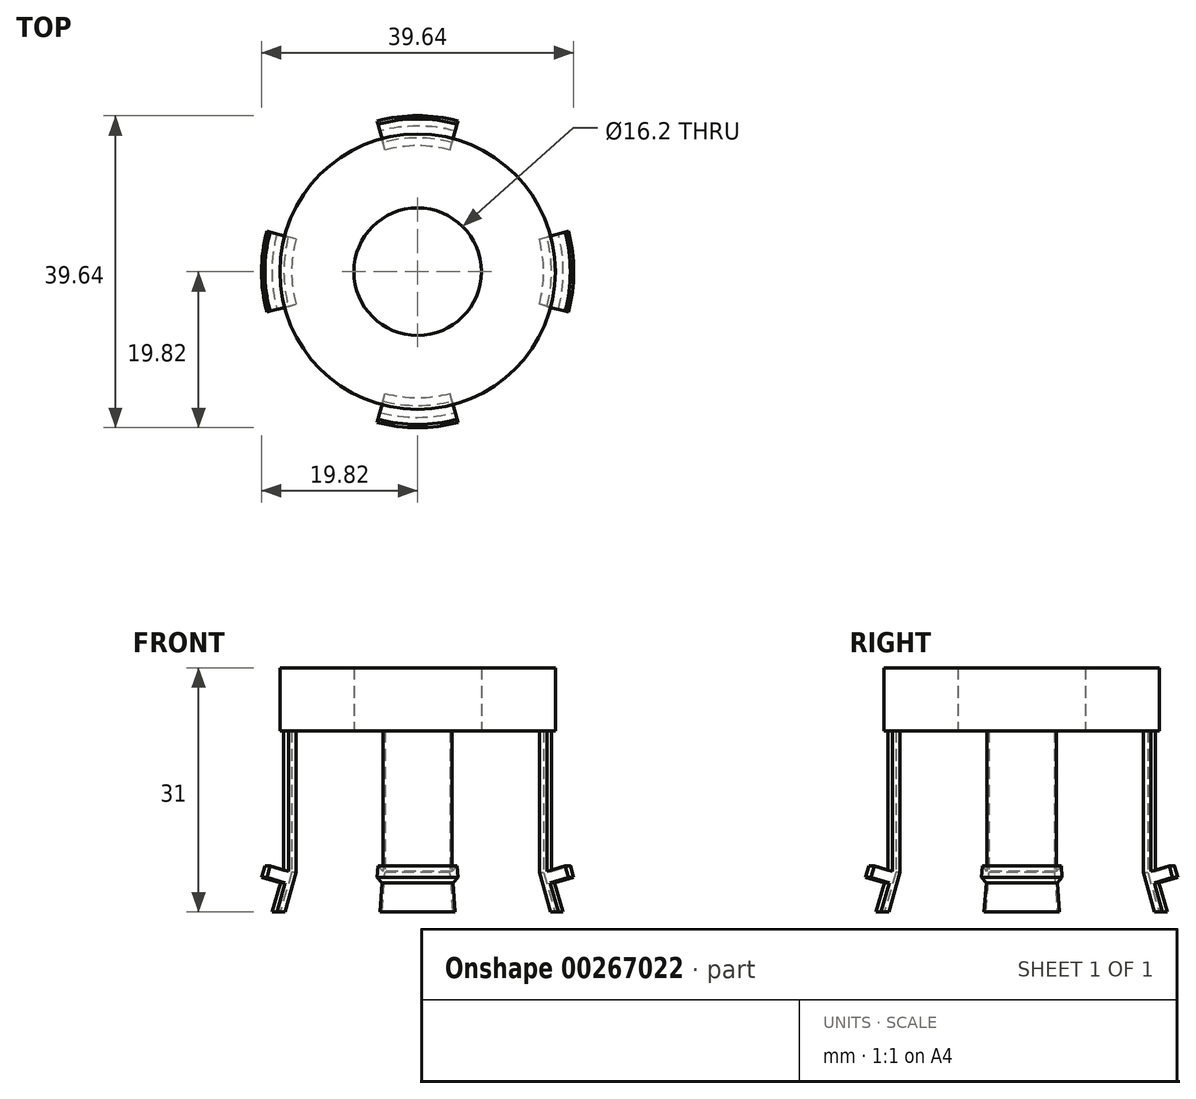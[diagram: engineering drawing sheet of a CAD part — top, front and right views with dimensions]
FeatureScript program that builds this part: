
annotation { "Feature Type Name" : "Feature", "Feature Type Description" : "" }
export const myFeature = defineFeature(function(context is Context, id is Id, definition is map)
    precondition{}
    {
        {
            var Q0;
            Q0=qCreatedBy(makeId("Front.planeOp"),FACE);
            var sketch = newSketch(context, id + "F0", { "sketchPlane" : qUnion([Q0])});
            skLineSegment(sketch, "E0", {"start": v(0, -11.42) * mm, "end": v(0, 25.7) * mm, "construction": true});
            skLineSegment(sketch, "E1", {"start": v(-16, 23) * mm, "end": v(-16, 5) * mm});
            skLineSegment(sketch, "E2", {"start": v(-16, 5) * mm, "end": v(-17.46, 0) * mm});
            skLineSegment(sketch, "E3", {"start": v(-17.46, 0) * mm, "end": v(-18.5, 0) * mm});
            skLineSegment(sketch, "E4", {"start": v(-18.5, 0) * mm, "end": v(-17, 5.14) * mm});
            skLineSegment(sketch, "E5", {"start": v(-17, 5.14) * mm, "end": v(-17, 23) * mm});
            skLineSegment(sketch, "E6", {"start": v(-17, 23) * mm, "end": v(-16, 23) * mm});
            skLineSegment(sketch, "E7", {"start": v(-17, 5.14) * mm, "end": v(-19.4, 5.84) * mm});
            skLineSegment(sketch, "E8", {"start": v(-19.4, 5.84) * mm, "end": v(-19.82, 4.4) * mm});
            skLineSegment(sketch, "E9", {"start": v(-19.82, 4.4) * mm, "end": v(-17.42, 3.7) * mm});
            skSolve(sketch);
        }
        {
            var Q0;
            Q0 = qSketchRegion(id + "F0", true);
            var Q1;
            Q1=sQuery(id+"F0.wireOp",EDGE,"E0");
            revolve(context, id + "F1", {"entities" : qUnion([Q0]), "axis" : qUnion([Q1]), "revolveType" : RevolveType.FULL});
        }
        {
            var Q0;
            Q0=makeQuery(id+"F1.opRevolve","SWEPT_FACE",FACE,{"disambiguationData":[OSD([sQuery(id+"F0.wireOp",EDGE,"E6")])]});
            var sketch = newSketch(context, id + "F2", { "sketchPlane" : qUnion([Q0])});
            skCircle(sketch, "E10", {"center": v(0, 0) * mm, "radius": 17.5 * mm});
            skCircle(sketch, "E11", {"center": v(0, 0) * mm, "radius": 8.1 * mm});
            skSolve(sketch);
        }
        {
            var Q0;
            Q0 = qSketchRegion(id + "F2", true);
            extrude(context, id + "F3", {"entities" : qUnion([Q0]), "operationType" : NewBodyOperationType.ADD, "depth" : 8 * mm});
        }
        {
            var Q0;
            Q0=qCreatedBy(makeId("Top.planeOp"),FACE);
            var sketch = newSketch(context, id + "F4", { "sketchPlane" : qUnion([Q0])});
            skArc(sketch, "E12", {"start": v(-21.73, -5.82) * mm, "mid": v(-15.9, -15.9) * mm, "end": v(-5.82, -21.73) * mm});
            skLineSegment(sketch, "E13", {"start": v(-5.82, -21.73) * mm, "end": v(5.82, 21.73) * mm});
            skLineSegment(sketch, "E14", {"start": v(5.82, -21.73) * mm, "end": v(-5.82, 21.73) * mm});
            skLineSegment(sketch, "E15", {"start": v(-21.73, -5.82) * mm, "end": v(21.73, 5.82) * mm});
            skLineSegment(sketch, "E16", {"start": v(21.73, -5.82) * mm, "end": v(-21.73, 5.82) * mm});
            skArc(sketch, "E17.trimOffspring", {"start": v(-5.82, 21.73) * mm, "mid": v(-15.9, 15.9) * mm, "end": v(-21.73, 5.82) * mm});
            skArc(sketch, "E18.trimOffspring", {"start": v(21.73, 5.82) * mm, "mid": v(15.9, 15.9) * mm, "end": v(5.82, 21.73) * mm});
            skArc(sketch, "E19.trimOffspring", {"start": v(5.82, -21.73) * mm, "mid": v(15.9, -15.9) * mm, "end": v(21.73, -5.82) * mm});
            skSolve(sketch);
        }
        {
            var Q0;
            Q0 = qSketchRegion(id + "F4", true);
            var Q1;
            {var subQ0=sQuery(id+"F2.wireOp",EDGE,"E10");Q1=makeQuery(id+"F3.boolean.opBoolean","SPLIT",FACE,{"disambiguationData":[TD([makeQuery(id+"F1.opRevolve","SWEPT_FACE",FACE,{"disambiguationData":[OSD([sQuery(id+"F0.wireOp",EDGE,"E5")])]})])],"derivedFrom":makeQuery(id+"F3.opExtrude","CAP_FACE",FACE,{"disambiguationData":[OSD([subQ0,sQuery(id+"F2.wireOp",EDGE,"E11")])],"isStart":true})});}
            extrude(context, id + "F5", {"entities" : qUnion([Q0]), "operationType" : NewBodyOperationType.REMOVE, "endBound" : BoundingType.UP_TO_SURFACE, "endBoundEntityFace" : qUnion([Q1]), "depth" : 20 * mm});
        }
    });
